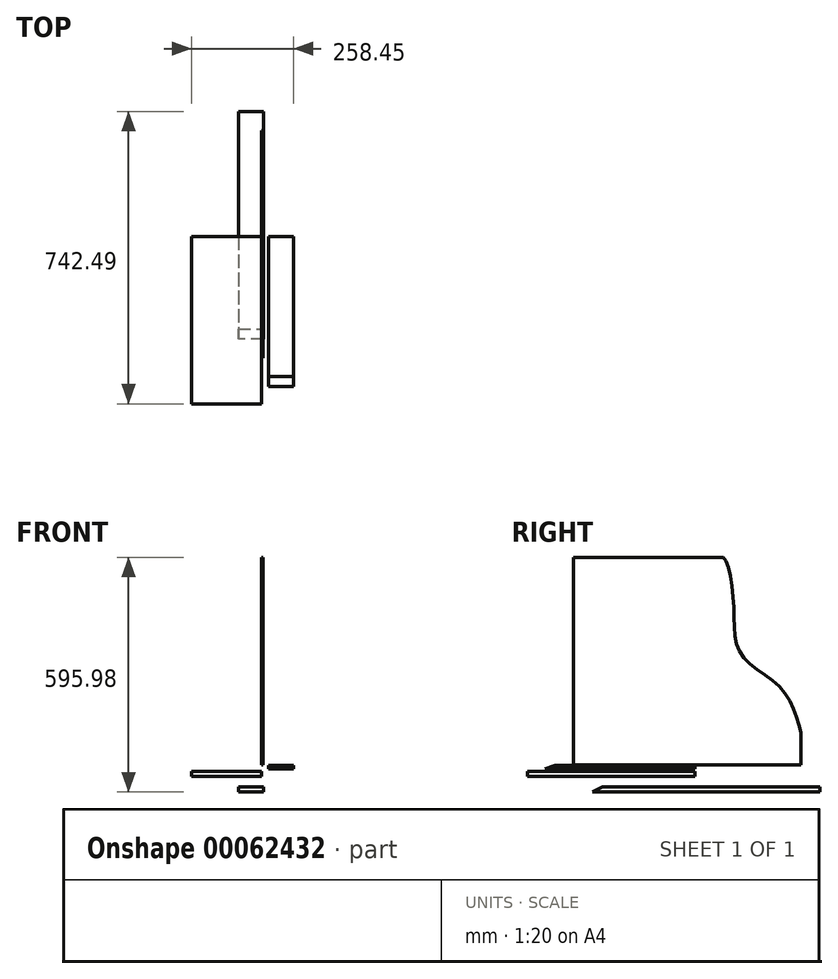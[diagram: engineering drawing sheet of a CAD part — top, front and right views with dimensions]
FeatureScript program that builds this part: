
annotation { "Feature Type Name" : "Feature", "Feature Type Description" : "" }
export const myFeature = defineFeature(function(context is Context, id is Id, definition is map)
    precondition{}
    {
        {
            var Q0;
            Q0=qCreatedBy(makeId("Top.planeOp"),FACE);
            var sketch = newSketch(context, id + "F0", { "sketchPlane" : qUnion([Q0])});
            skLineSegment(sketch, "E0.bottom", {"start": v(4.81, 317.04) * mm, "end": v(-58.69, 317.04) * mm});
            skLineSegment(sketch, "E0.top", {"start": v(4.81, -260.81) * mm, "end": v(-58.69, -260.81) * mm});
            skLineSegment(sketch, "E0.left", {"start": v(4.81, 317.04) * mm, "end": v(4.81, -260.81) * mm});
            skLineSegment(sketch, "E0.right", {"start": v(-58.69, 317.04) * mm, "end": v(-58.69, -260.81) * mm});
            skSolve(sketch);
        }
        {
            var Q0;
            Q0=makeQuery(id+"F0.imprint","IMPRINT",FACE,{"disambiguationData":[TD([[makeQuery(id+"F0.imprint","IMPRINT",EDGE,{"derivedFrom":sQuery(id+"F0.wireOp",EDGE,"E0.bottom")}),1.0]])]});
            extrude(context, id + "F1", {"entities" : qUnion([Q0]), "depth" : 12.7 * mm});
        }
        {
            var Q0;
            Q0=qCreatedBy(makeId("Right.planeOp"),FACE);
            var sketch = newSketch(context, id + "F2", { "sketchPlane" : qUnion([Q0])});
            skLineSegment(sketch, "E1.bottom", {"start": v(-309.27, 68.93) * mm, "end": v(268.58, 68.93) * mm});
            skLineSegment(sketch, "E1.top", {"start": v(-309.27, 595.98) * mm, "end": v(268.58, 595.98) * mm});
            skLineSegment(sketch, "E1.left", {"start": v(-309.27, 68.93) * mm, "end": v(-309.27, 595.98) * mm});
            skLineSegment(sketch, "E1.right", {"start": v(268.58, 68.93) * mm, "end": v(268.58, 595.98) * mm});
            skSolve(sketch);
        }
        {
            var Q0;
            Q0=makeQuery(id+"F2.imprint","IMPRINT",FACE,{"disambiguationData":[TD([[makeQuery(id+"F2.imprint","IMPRINT",EDGE,{"derivedFrom":sQuery(id+"F2.wireOp",EDGE,"E1.bottom")}),1.0]])]});
            extrude(context, id + "F3", {"entities" : qUnion([Q0]), "depth" : 3.17 * mm});
        }
        {
            var Q0;
            Q0=makeQuery(id+"F3.opExtrude","CAP_FACE",FACE,{"disambiguationData":[OSD([sQuery(id+"F2.wireOp",EDGE,"E1.bottom"),sQuery(id+"F2.wireOp",EDGE,"E1.top"),sQuery(id+"F2.wireOp",EDGE,"E1.left"),sQuery(id+"F2.wireOp",EDGE,"E1.right")])],"isStart":false});
            var sketch = newSketch(context, id + "F4", { "sketchPlane" : qUnion([Q0])});
            skLineSegment(sketch, "E2", {"start": v(268.58, 213.3) * mm, "end": v(268.58, 595.98) * mm});
            skLineSegment(sketch, "E3", {"start": v(268.58, 595.98) * mm, "end": v(71.73, 595.98) * mm});
            skFitSpline(sketch, "E4", {"points": [v(268.58, 151.34) * mm, v(220.7, 260.65) * mm, v(117.65, 350.28) * mm, v(98.1, 479.43) * mm, v(71.73, 595.98) * mm], "startDerivative": vector(-105.3, 434.64) * mm, "endDerivative": vector(-160.88, 101.17) * mm});
            skLineSegment(sketch, "E5", {"start": v(268.58, 213.3) * mm, "end": v(268.58, 151.34) * mm});
            skSolve(sketch);
        }
        {
            var Q0;
            Q0 = qSketchRegion(id + "F4", true);
            extrude(context, id + "F5", {"entities" : qUnion([Q0]), "operationType" : NewBodyOperationType.REMOVE, "oppositeDirection" : true, "depth" : 25.4 * mm});
        }
        {
            var Q0;
            Q0=makeQuery(id+"F1.opExtrude","SWEPT_FACE",FACE,{"disambiguationData":[OSD([sQuery(id+"F0.wireOp",EDGE,"E0.left")])]});
            var sketch = newSketch(context, id + "F6", { "sketchPlane" : qUnion([Q0])});
            skLineSegment(sketch, "E6", {"start": v(-260.81, 0) * mm, "end": v(-235.41, 12.7) * mm});
            skLineSegment(sketch, "E7", {"start": v(-235.41, 12.7) * mm, "end": v(-260.81, 12.7) * mm});
            skLineSegment(sketch, "E8", {"start": v(-260.81, 12.7) * mm, "end": v(-260.81, 0) * mm});
            skSolve(sketch);
        }
        {
            var Q0;
            Q0 = qSketchRegion(id + "F6", true);
            extrude(context, id + "F7", {"entities" : qUnion([Q0]), "operationType" : NewBodyOperationType.REMOVE, "endBound" : BoundingType.THROUGH_ALL, "oppositeDirection" : true, "depth" : 25.4 * mm});
        }
        {
            var Q0;
            Q0 = qSketchRegion(id + "F4", true);
            extrude(context, id + "F8", {"entities" : qUnion([Q0]), "operationType" : NewBodyOperationType.REMOVE, "endBound" : BoundingType.THROUGH_ALL, "oppositeDirection" : true, "depth" : 25.4 * mm});
        }
        {
            var Q0;
            Q0 = qSketchRegion(id + "F4", true);
            extrude(context, id + "F9", {"entities" : qUnion([Q0]), "operationType" : NewBodyOperationType.REMOVE, "endBound" : BoundingType.THROUGH_ALL, "oppositeDirection" : true, "depth" : 25.4 * mm});
        }
        {
            var Q0;
            Q0=qCreatedBy(makeId("Front.planeOp"),FACE);
            var sketch = newSketch(context, id + "F10", { "sketchPlane" : qUnion([Q0])});
            skLineSegment(sketch, "E9.bottom", {"start": v(0, 40.13) * mm, "end": v(-177.8, 40.13) * mm});
            skLineSegment(sketch, "E9.top", {"start": v(0, 52.83) * mm, "end": v(-177.8, 52.83) * mm});
            skLineSegment(sketch, "E9.left", {"start": v(0, 40.13) * mm, "end": v(0, 52.83) * mm});
            skLineSegment(sketch, "E9.right", {"start": v(-177.8, 40.13) * mm, "end": v(-177.8, 52.83) * mm});
            skSolve(sketch);
        }
        {
            var Q0;
            Q0 = qSketchRegion(id + "F10", true);
            extrude(context, id + "F11", {"entities" : qUnion([Q0]), "depth" : 425.45 * mm});
        }
        {
            var Q0;
            Q0=makeQuery(id+"F1.opExtrude","SWEPT_BODY",BODY,{"disambiguationData":[OSD([sQuery(id+"F0.wireOp",EDGE,"E0.bottom"),sQuery(id+"F0.wireOp",EDGE,"E0.top"),sQuery(id+"F0.wireOp",EDGE,"E0.left"),sQuery(id+"F0.wireOp",EDGE,"E0.right")])]});
            transform(context, id + "F12", {"entities" : qUnion([Q0]), "transformType" : TransformType.TRANSLATION_3D, "dx" : 127 * mm, "dy" : 0 * mm, "dz" : 0 * mm, "makeCopy" : true});
        }
        {
            var Q0;
            Q0=makeQuery(id+"F12.opPattern","COPY",BODY,{"derivedFrom":makeQuery(id+"F1.opExtrude","SWEPT_BODY",BODY,{"disambiguationData":[OSD([sQuery(id+"F0.wireOp",EDGE,"E0.bottom"),sQuery(id+"F0.wireOp",EDGE,"E0.top"),sQuery(id+"F0.wireOp",EDGE,"E0.left"),sQuery(id+"F0.wireOp",EDGE,"E0.right")])]}),"instanceName":"1"});
            deleteBodies(context, id + "F13", {"entities" : qUnion([Q0])});
        }
        {
            var Q0;
            Q0=qCreatedBy(makeId("Front.planeOp"),FACE);
            var sketch = newSketch(context, id + "F14", { "sketchPlane" : qUnion([Q0])});
            skLineSegment(sketch, "E10.bottom", {"start": v(17.15, 68) * mm, "end": v(80.65, 68) * mm});
            skLineSegment(sketch, "E10.top", {"start": v(17.15, 58.47) * mm, "end": v(80.65, 58.47) * mm});
            skLineSegment(sketch, "E10.left", {"start": v(17.15, 68) * mm, "end": v(17.15, 58.47) * mm});
            skLineSegment(sketch, "E10.right", {"start": v(80.65, 68) * mm, "end": v(80.65, 58.47) * mm});
            skSolve(sketch);
        }
        {
            var Q0;
            Q0 = qSketchRegion(id + "F14", true);
            extrude(context, id + "F15", {"entities" : qUnion([Q0]), "depth" : 381 * mm});
        }
        {
            var Q0;
            Q0=makeQuery(id+"F15.opExtrude","SWEPT_FACE",FACE,{"disambiguationData":[OSD([sQuery(id+"F14.wireOp",EDGE,"E10.right")])]});
            var sketch = newSketch(context, id + "F16", { "sketchPlane" : qUnion([Q0])});
            skLineSegment(sketch, "E11", {"start": v(-381, 58.47) * mm, "end": v(-355.6, 68) * mm});
            skLineSegment(sketch, "E12", {"start": v(-355.6, 68) * mm, "end": v(-381, 68) * mm});
            skLineSegment(sketch, "E13", {"start": v(-381, 68) * mm, "end": v(-381, 58.47) * mm});
            skSolve(sketch);
        }
        {
            var Q0;
            Q0 = qSketchRegion(id + "F16", true);
            extrude(context, id + "F17", {"entities" : qUnion([Q0]), "operationType" : NewBodyOperationType.REMOVE, "endBound" : BoundingType.THROUGH_ALL, "oppositeDirection" : true, "depth" : 25.4 * mm});
        }
    });
